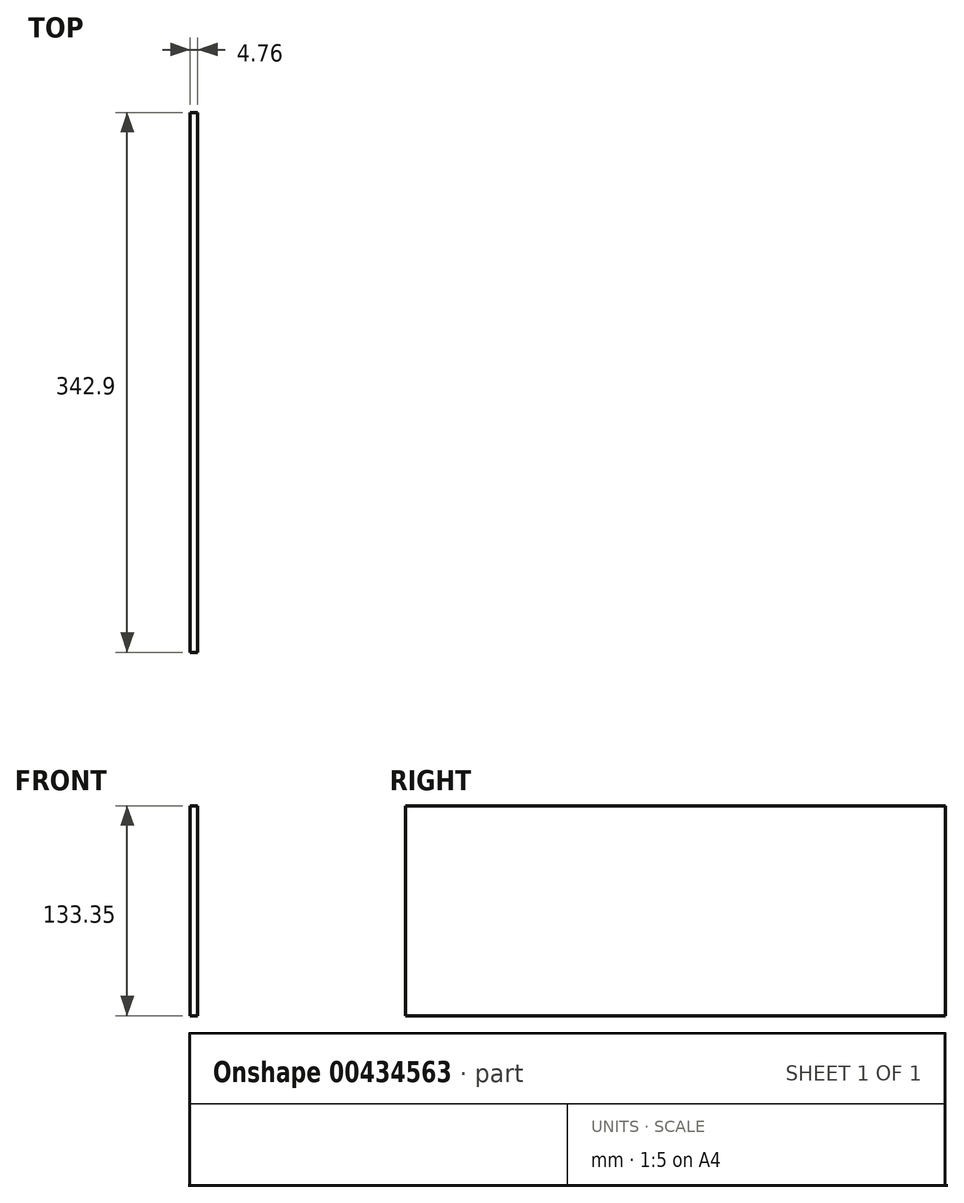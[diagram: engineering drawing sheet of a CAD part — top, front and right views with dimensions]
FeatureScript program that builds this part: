
annotation { "Feature Type Name" : "Feature", "Feature Type Description" : "" }
export const myFeature = defineFeature(function(context is Context, id is Id, definition is map)
    precondition{}
    {
        {
            var Q0;
            Q0=qCreatedBy(makeId("Right.planeOp"),FACE);
            var sketch = newSketch(context, id + "F0", { "sketchPlane" : qUnion([Q0])});
            skLineSegment(sketch, "E0.bottom", {"start": v(-91.13, 77.1) * mm, "end": v(251.77, 77.1) * mm});
            skLineSegment(sketch, "E0.top", {"start": v(-91.13, -56.24) * mm, "end": v(251.77, -56.24) * mm});
            skLineSegment(sketch, "E0.left", {"start": v(-91.13, 77.1) * mm, "end": v(-91.13, -56.24) * mm});
            skLineSegment(sketch, "E0.right", {"start": v(251.77, 77.1) * mm, "end": v(251.77, -56.24) * mm});
            skSolve(sketch);
        }
        {
            var Q0;
            Q0=makeQuery(id+"F0.imprint","IMPRINT",FACE,{"disambiguationData":[TD([[makeQuery(id+"F0.imprint","IMPRINT",EDGE,{"derivedFrom":sQuery(id+"F0.wireOp",EDGE,"E0.bottom")}),-1.0]])]});
            extrude(context, id + "F1", {"entities" : qUnion([Q0]), "depth" : 4.76 * mm});
        }
    });
